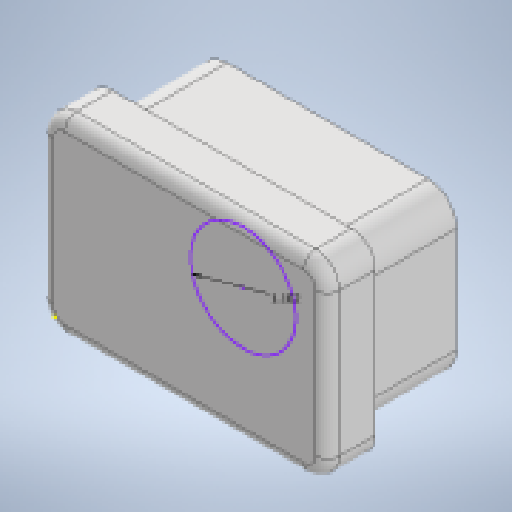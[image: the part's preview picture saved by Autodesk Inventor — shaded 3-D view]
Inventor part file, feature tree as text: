
AUTODESK INVENTOR PART (.ipt)
format: ipt  version: 2023 (Build 270158000, 158)  size: 198,656 bytes
history: native  units: in
note: dims shown in document units (in); Inventor stores cm internally (conversion verified against a paired STEP export)
features: extrude x3, sketch x3, fillet x1
ambient origin geometry x8: Origin, YZ Plane, XZ Plane, XY Plane, X Axis, Y Axis, Z Axis, Center Point
bodies: Solid1 (feature_tree)
feature tree (7):
  extrude  "Extrusion1"  Depth=1.7in
  extrude  "Extrusion2"  Depth=1.0in TaperAngle=0.0deg
  fillet  "Fillet1"  Radius=3.0in
  extrude  "Extrusion3"  Depth=0.25in
  sketch  "Sketch1"  dims[d0=2.7in d1=1.7in]
  sketch  "Sketch2"  dims[d3=0.3in d4=1.0in d5=0.0in d6=3.0in]
  sketch  "Sketch3"  dims[d7=2.0in d8=0.25in d9=0.5in d10=0.0in d11=0.125in d12=1.1417in d13=1.4961in d14=0.1811in d15=45.0deg d16=0.5in d17=0.0in]
